FCSTD DOCUMENT  (FreeCAD 1.1R20260414 (Git shallow))
Label: OutlineA
License: All rights reserved
LicenseURL: https://en.wikipedia.org/wiki/All_rights_reserved
objects: App::Point×1, Sketcher::SketchObject×1, PartDesign::Body×1
note: 3 computed .brp shape members not serialized (recipe doc carries the construction recipe); baked Part::Feature solids carry a one-line shape summary decoded from their .brp

FEATURE [App::Point] Origin001
  Role = Origin
FEATURE [Sketcher::SketchObject] Sketch
  ArcFitTolerance = 1e-06
  AttachmentSupport = -> [Origin]
  ExternalTypes = [0]
  FullyConstrained = true
  MakeInternals = false
  MapMode = 5
  _ExternalGeoVersion = 1
  sketch-geometry (6):
    g0: ArcOfCircle CenterX=0 CenterY=3 CenterZ=0 NormalX=0 NormalY=0 NormalZ=1 AngleXU=0 Radius=13 StartAngle=1e-16 EndAngle=3.14159
    g1: ArcOfCircle CenterX=0 CenterY=-3 CenterZ=0 NormalX=0 NormalY=0 NormalZ=1 AngleXU=0 Radius=13 StartAngle=3.14159 EndAngle=6.28319
    g2: LineSegment StartX=13 StartY=3 StartZ=0 EndX=13 EndY=-3 EndZ=0
    g3: LineSegment StartX=-13 StartY=3 StartZ=0 EndX=-13 EndY=-3 EndZ=0
    g4: GeomPoint X=0 Y=16 Z=0
    g5: GeomPoint X=0 Y=-16 Z=0
  constraints (13):
    c: Tangent(g0,g2) = 1.5708
    c: Tangent(g0,g3) = -1.5708
    c: Tangent(g1,g2) = 1.5708
    c: Tangent(g1,g3) = -1.5708
    c: Equal(g0,g1)
    c: Symmetric(g0,g1,g-1)
    c: PointOnObject(g0,g-2)
    c: PointOnObject(g4,g0)
    c: PointOnObject(g5,g1)
    c: PointOnObject(g4,g-2)
    c: PointOnObject(g5,g-2)
    c: DistanceY(g-1,g4) = 16
    c: DistanceX(g0,g0) = 26
FEATURE [PartDesign::Body] Body
  AllowCompound = true
  Group = -> [Sketch]
  Origin = -> Origin
